FCSTD DOCUMENT  (FreeCAD 0.18R4 (GitTag))
Label: lib_obras_civiles_aeth
License: All rights reserved
LicenseURL: http://en.wikipedia.org/wiki/All_rights_reserved
objects: Part::Part2DObjectPython×84, App::Part×42, App::FeaturePython×21, App::DocumentObjectGroup×11, Spreadsheet::Sheet×4, Part::FeaturePython×4
note: 88 computed .brp shape members not serialized (recipe doc carries the construction recipe); baked Part::Feature solids carry a one-line shape summary decoded from their .brp

FEATURE [Part::Part2DObjectPython] Line001  # Draft 2D object (typed FeaturePython)
  ChamferSize = 0
  Closed = false
  End = (-48.8237,-10,0)
  FilletRadius = 0
  Length = 128.824
  MakeFace = false
  Placement = pos=(80,-10,0) rot=(0,0,1;0rad)
  Points = (2) [(0,-5.32907e-15,0),(-128.824,-3.55271e-15,0)]
  Start = (80,-10,0)
  Subdivisions = 0
FEATURE [Part::Part2DObjectPython] Line  # Draft 2D object (typed FeaturePython)
  ChamferSize = 0
  Closed = false
  End = (-48.9007,10,0)
  FilletRadius = 0
  Length = 128.901
  MakeFace = false
  Placement = pos=(80,10,0) rot=(0,0,1;0rad)
  Points = (2) [(0,0,0),(-128.901,-3.55271e-15,0)]
  Start = (80,10,0)
  Subdivisions = 0
FEATURE [Part::Part2DObjectPython] Circle  # Draft 2D object (typed FeaturePython)
  FirstAngle = 0
  LastAngle = 0
  MakeFace = false
  Radius = 50
FEATURE [Part::Part2DObjectPython] Line003  # Draft 2D object (typed FeaturePython)
  ChamferSize = 0
  Closed = false
  End = (100,100,0)
  FilletRadius = 0
  Length = 91.7357
  MakeFace = false
  Placement = pos=(35.1355,35.1306,0) rot=(0,0,1;0rad)
  Points = (2) [(0,0,0),(64.8645,64.8694,0)]
  Start = (35.1355,35.1306,0)
  Subdivisions = 0
FEATURE [Part::Part2DObjectPython] Rectangle016  label="puerta"  # Draft 2D object (typed FeaturePython)
  ChamferSize = 0
  Columns = 1
  FilletRadius = 0
  Height = 50
  Length = 900
  MakeFace = true
  Rows = 1
FEATURE [Part::Part2DObjectPython] Line004  label="limite_apertura_puerta"  # Draft 2D object (typed FeaturePython)
  ChamferSize = 0
  Closed = false
  End = (0,900,0)
  FilletRadius = 0
  Length = 900
  MakeFace = true
  Points = (2) [(0,0,0),(2.75546e-14,900,0)]
  Start = (0,0,0)
  Subdivisions = 0
FEATURE [Part::Part2DObjectPython] Arc  label="apertura_puerta"  # Draft 2D object (typed FeaturePython)
  FirstAngle = 0
  LastAngle = 90
  MakeFace = true
  Radius = 900
FEATURE [App::DocumentObjectGroup] Group001  label="puerta_generica"
  Group = -> [Rectangle016,Line004,Arc]
FEATURE [App::Part] Part002  label="puerta_90cm__"
  Group = -> [Arc,Rectangle016,Line004,Group001]
  Origin = -> Origin002
FEATURE [Part::Part2DObjectPython] Rectangle017  label="puerta_doble_cuerpo"  # Draft 2D object (typed FeaturePython)
  ChamferSize = 0
  Columns = 1
  FilletRadius = 0
  Height = 50
  Length = 2000
  MakeFace = true
  Rows = 1
FEATURE [Part::Part2DObjectPython] Line005  label="puerta_li"  # Draft 2D object (typed FeaturePython)
  ChamferSize = 0
  Closed = false
  End = (0,1000,0)
  FilletRadius = 0
  Length = 1000
  MakeFace = true
  Points = (2) [(0,0,0),(3.06162e-14,1000,0)]
  Start = (0,0,0)
  Subdivisions = 0
FEATURE [Part::Part2DObjectPython] Line006  label="puerta_ld"  # Draft 2D object (typed FeaturePython)
  ChamferSize = 0
  Closed = false
  End = (2000,1000,0)
  FilletRadius = 0
  Length = 1000
  MakeFace = true
  Placement = pos=(2000,6.12e-14,0) rot=(0,0,1;0rad)
  Points = (2) [(0,0,0),(0,1000,0)]
  Start = (2000,6.12e-14,0)
  Subdivisions = 0
FEATURE [Part::Part2DObjectPython] Arc001  label="arco_ld"  # Draft 2D object (typed FeaturePython)
  FirstAngle = 90
  LastAngle = 180
  MakeFace = true
  Placement = pos=(2000,6.12e-14,0) rot=(0,0,1;0rad)
  Radius = 1000
FEATURE [Part::Part2DObjectPython] Arc002  label="arco_li"  # Draft 2D object (typed FeaturePython)
  FirstAngle = 0
  LastAngle = 90
  MakeFace = true
  Radius = 1000
FEATURE [App::DocumentObjectGroup] Group002  label="puerta_generica_doble"
  Group = -> [Rectangle017,Line005,Line006,Arc001,Arc002]
FEATURE [App::Part] Part003  label="puerta_doble_2m__"
  Group = -> [Rectangle017,Line006,Line005,Arc001,Arc002,Group002]
  Origin = -> Origin003
FEATURE [Part::Part2DObjectPython] Wire001  # Draft 2D object (typed FeaturePython)
  ChamferSize = 0
  Closed = true
  End = (300,100,0)
  FilletRadius = 0
  Length = 716.228
  MakeFace = true
  Points = (3) [(0,0,0),(300,9.18485e-15,0),(300,100,0)]
  Start = (0,0,0)
  Subdivisions = 0
FEATURE [Part::Part2DObjectPython] Wire002  # Draft 2D object (typed FeaturePython)
  ChamferSize = 0
  Closed = true
  End = (300,100,0)
  FilletRadius = 0
  Length = 716.228
  MakeFace = true
  Points = (3) [(0,0,0),(3.06162e-15,100,0),(300,100,0)]
  Start = (0,0,0)
  Subdivisions = 0
FEATURE [Part::Part2DObjectPython] Rectangle039  # Draft 2D object (typed FeaturePython)
  ChamferSize = 0
  Columns = 1
  FilletRadius = 0
  Height = 100
  Length = 100
  MakeFace = true
  Rows = 1
FEATURE [Spreadsheet::Sheet] IfcProperties005  label="caja_2400_df_props"
  cells = A1=parametro; B1=magnitud; C1=unidades; A2=tipo_toma; B2=ciega; C2=n/a; A3=estado; B3=ok; C3=n/a; A4=num_circuito; C4=n/a; A5=num_tablero_distribucion; C5=n/a; A6=altura_desde_piso; C6=m
FEATURE [Part::Part2DObjectPython] Circle007  # Draft 2D object (typed FeaturePython)
  FirstAngle = 0
  LastAngle = 0
  MakeFace = false
  Radius = 50
FEATURE [Part::Part2DObjectPython] Line019  # Draft 2D object (typed FeaturePython)
  ChamferSize = 0
  Closed = false
  End = (-48.9007,10,0)
  FilletRadius = 0
  Length = 128.901
  MakeFace = false
  Placement = pos=(80,10,0) rot=(0,0,1;0rad)
  Points = (2) [(0,0,0),(-128.901,-3.55271e-15,0)]
  Start = (80,10,0)
  Subdivisions = 0
FEATURE [Part::Part2DObjectPython] Line020  # Draft 2D object (typed FeaturePython)
  ChamferSize = 0
  Closed = false
  End = (-48.8237,-10,0)
  FilletRadius = 0
  Length = 128.824
  MakeFace = false
  Placement = pos=(80,-10,0) rot=(0,0,1;0rad)
  Points = (2) [(0,-5.32907e-15,0),(-128.824,-3.55271e-15,0)]
  Start = (80,-10,0)
  Subdivisions = 0
FEATURE [Spreadsheet::Sheet] IfcProperties012  label="tomacorriente_interruptor_props"
  cells = A1=parametro; B1=magnitud; C1=unidades; A2=tipo_toma; C2=n/a; A3=estado; C3=n/a; A4=num_circuito_toma; C4=n/a; A5=num_circuito_interruptor; C5=n/a; A6=num_tablero_distribucion_toma; C6=n/a; A7=num_tablero_distribucion_interruptor; C7=n/a; A8=altura_desde_piso; C8=m
FEATURE [Part::Part2DObjectPython] Line021  # Draft 2D object (typed FeaturePython)
  ChamferSize = 0
  Closed = false
  End = (250,100,0)
  FilletRadius = 0
  Length = 91.7357
  MakeFace = false
  Placement = pos=(185.136,35.1306,0) rot=(0,0,1;0rad)
  Points = (2) [(0,0,0),(64.8645,64.8694,0)]
  Start = (185.136,35.1306,0)
  Subdivisions = 0
FEATURE [Part::Part2DObjectPython] Circle008  # Draft 2D object (typed FeaturePython)
  FirstAngle = 0
  LastAngle = 0
  MakeFace = false
  Placement = pos=(150,0,0) rot=(0,0,1;0rad)
  Radius = 50
FEATURE [Part::Part2DObjectPython] Line025  # Draft 2D object (typed FeaturePython)
  ChamferSize = 0
  Closed = false
  End = (100,100,0)
  FilletRadius = 0
  Length = 91.7357
  MakeFace = false
  Placement = pos=(35.1355,35.1306,0) rot=(0,0,1;0rad)
  Points = (2) [(0,0,0),(64.8645,64.8694,0)]
  Start = (35.1355,35.1306,0)
  Subdivisions = 0
FEATURE [Part::Part2DObjectPython] Circle011  # Draft 2D object (typed FeaturePython)
  FirstAngle = 0
  LastAngle = 0
  MakeFace = false
  Radius = 100
FEATURE [Part::Part2DObjectPython] Line028  # Draft 2D object (typed FeaturePython)
  ChamferSize = 0
  Closed = false
  End = (0,-100,0)
  FilletRadius = 0
  Length = 200
  MakeFace = true
  Placement = pos=(0,100,0) rot=(0,0,1;0rad)
  Points = (2) [(0,0,0),(0,-200,0)]
  Start = (0,100,0)
  Subdivisions = 0
FEATURE [Part::Part2DObjectPython] Line029  # Draft 2D object (typed FeaturePython)
  ChamferSize = 0
  Closed = false
  End = (-100,3.8e-15,0)
  FilletRadius = 0
  Length = 200
  MakeFace = true
  Placement = pos=(100,1.8e-14,0) rot=(0,0,1;0rad)
  Points = (2) [(0,0,0),(-200,-1.42109e-14,0)]
  Start = (100,1.8e-14,0)
  Subdivisions = 0
FEATURE [Part::Part2DObjectPython] Line035  # Draft 2D object (typed FeaturePython)
  ChamferSize = 0
  Closed = false
  End = (0,0,0)
  FilletRadius = 0
  Length = 200
  MakeFace = true
  Placement = pos=(0,200,0) rot=(0,0,1;0rad)
  Points = (2) [(0,0,0),(0,-200,0)]
  Start = (0,200,0)
  Subdivisions = 0
FEATURE [Part::Part2DObjectPython] Arc003  # Draft 2D object (typed FeaturePython)
  FirstAngle = -90
  LastAngle = 90
  MakeFace = true
  Placement = pos=(0,100,0) rot=(0,0,1;0rad)
  Radius = 100
FEATURE [Part::Part2DObjectPython] Line036  # Draft 2D object (typed FeaturePython)
  ChamferSize = 0
  Closed = false
  End = (200,300,0)
  FilletRadius = 0
  Length = 141.421
  MakeFace = true
  Placement = pos=(100,200,0) rot=(0,0,1;0rad)
  Points = (2) [(0,0,0),(100,100,0)]
  Start = (100,200,0)
  Subdivisions = 0
FEATURE [Part::Part2DObjectPython] Line037  # Draft 2D object (typed FeaturePython)
  ChamferSize = 0
  Closed = false
  End = (200,-100,0)
  FilletRadius = 0
  Length = 141.421
  MakeFace = true
  Placement = pos=(100,6.1e-15,0) rot=(0,0,1;0rad)
  Points = (2) [(0,0,0),(100,-100,0)]
  Start = (100,6.1e-15,0)
  Subdivisions = 0
FEATURE [Part::Part2DObjectPython] Line038  # Draft 2D object (typed FeaturePython)
  ChamferSize = 0
  Closed = false
  End = (300,100,0)
  FilletRadius = 0
  Length = 100
  MakeFace = true
  Placement = pos=(200,100,0) rot=(0,0,1;0rad)
  Points = (2) [(0,0,0),(100,-5.68434e-14,0)]
  Start = (200,100,0)
  Subdivisions = 0
FEATURE [App::DocumentObjectGroup] Grupo027  label="caja_2400_df_generica"
  Group = -> [Rectangle039,IfcProperties005]
FEATURE [App::Part] Part009  label="caja_2400_df__"
  Group = -> [Rectangle039,Grupo027,IfcProperties005]
  Origin = -> Origin009
FEATURE [Part::Part2DObjectPython] Rectangle041  # Draft 2D object (typed FeaturePython)
  ChamferSize = 0
  Columns = 1
  FilletRadius = 0
  Height = 60
  Length = 100
  MakeFace = true
  Rows = 1
FEATURE [Spreadsheet::Sheet] IfcProperties037  label="caja_5800_props"
  cells = A1=parametro; B1=magnitud; C1=unidades; A2=tipo_toma; B2=ciega; C2=n/a; A3=estado; B3=n/d; C3=n/a; A4=num_circuito; B4=n/d; C4=n/a; A5=num_tablero_distribucion; B5=n/d; C5=n/a; A6=altura_desde_piso; C6=m
FEATURE [App::DocumentObjectGroup] Grupo056  label="caja_5800_generica"
  Group = -> [Rectangle041,IfcProperties037]
FEATURE [App::Part] Part041  label="caja_5800___"
  Group = -> [Rectangle041,Grupo056,IfcProperties037]
  Origin = -> Origin041
FEATURE [Part::Part2DObjectPython] Rectangle043  # Draft 2D object (typed FeaturePython)
  ChamferSize = 0
  Columns = 1
  FilletRadius = 0
  Height = 100
  Length = 100
  MakeFace = true
  Rows = 1
FEATURE [Spreadsheet::Sheet] IfcProperties039  label="caja_2400_props"
  cells = A1=parametro; B1=magnitud; C1=unidades; A2=tipo_toma; B2=ciega; C2=n/a; A3=estado; B3=ok; C3=n/a; A4=num_circuito; C4=n/a; A5=num_tablero_distribucion; C5=n/a; A6=altura_desde_piso; C6=m
FEATURE [App::DocumentObjectGroup] Grupo058  label="caja_2400_generica"
  Group = -> [Rectangle043,IfcProperties039]
FEATURE [App::Part] Part043  label="caja_2400__"
  Group = -> [Rectangle043,Grupo058,IfcProperties039]
  Origin = -> Origin043
FEATURE [Part::Part2DObjectPython] Rectangle048  label="luz_30x120_cuerpo"  # Draft 2D object (typed FeaturePython)
  ChamferSize = 0
  Columns = 1
  FilletRadius = 0
  Height = 300
  Length = 1200
  MakeFace = true
  Rows = 1
FEATURE [Part::Part2DObjectPython] Circle051  # Draft 2D object (typed FeaturePython)
  FirstAngle = 0
  LastAngle = 0
  MakeFace = true
  Radius = 100
FEATURE [Part::Part2DObjectPython] Line124  # Draft 2D object (typed FeaturePython)
  ChamferSize = 0
  Closed = false
  End = (0,-100,0)
  FilletRadius = 0
  Length = 200
  MakeFace = true
  Placement = pos=(0,100,0) rot=(0,0,1;0rad)
  Points = (2) [(0,0,0),(0,-200,0)]
  Start = (0,100,0)
  Subdivisions = 0
FEATURE [Part::Part2DObjectPython] Line125  # Draft 2D object (typed FeaturePython)
  ChamferSize = 0
  Closed = false
  End = (-100,3.8e-15,0)
  FilletRadius = 0
  Length = 200
  MakeFace = true
  Placement = pos=(100,1.8e-14,0) rot=(0,0,1;0rad)
  Points = (2) [(0,0,0),(-200,-1.42109e-14,0)]
  Start = (100,1.8e-14,0)
  Subdivisions = 0
FEATURE [Part::Part2DObjectPython] Circle052  label="datos_techo_base"  # Draft 2D object (typed FeaturePython)
  FirstAngle = 0
  LastAngle = 0
  MakeFace = false
  Radius = 50
FEATURE [Part::Part2DObjectPython] Polygon  label="datos_base"  # Draft 2D object (typed FeaturePython)
  ChamferSize = 0
  DrawMode = 0
  FacesNumber = 3
  FilletRadius = 0
  MakeFace = true
  Placement = pos=(0,0,0) rot=(0,0,1;1.5708rad)
  Radius = 50.47
FEATURE [Part::Part2DObjectPython] Polygon001  label="datos_base001"  # Draft 2D object (typed FeaturePython)
  ChamferSize = 0
  DrawMode = 0
  FacesNumber = 3
  FilletRadius = 0
  MakeFace = true
  Placement = pos=(0,0,0) rot=(0,0,1;1.5708rad)
  Radius = 50.47
FEATURE [Part::Part2DObjectPython] Polygon002  label="datos_base002"  # Draft 2D object (typed FeaturePython)
  ChamferSize = 0
  DrawMode = 0
  FacesNumber = 3
  FilletRadius = 0
  MakeFace = true
  Placement = pos=(0,0,0) rot=(0,0,1;1.5708rad)
  Radius = 50.47
FEATURE [Part::Part2DObjectPython] Circle053  label="datos_techo_base001"  # Draft 2D object (typed FeaturePython)
  FirstAngle = 0
  LastAngle = 0
  MakeFace = false
  Radius = 50
FEATURE [App::Part] Part085  label="datos_techo__"
  Group = -> [Polygon002,Circle053]
  Origin = -> Origin085
FEATURE [Part::Part2DObjectPython] Rectangle  label="datos_piso_base"  # Draft 2D object (typed FeaturePython)
  ChamferSize = 0
  Columns = 1
  FilletRadius = 0
  Height = 100
  Length = 100
  MakeFace = false
  Placement = pos=(-50,-40,0) rot=(0,0,1;0rad)
  Rows = 1
FEATURE [App::DocumentObjectGroup] Group013  label="piezas_red_datos_base__"
  Group = -> [Polygon,Circle052,Rectangle]
FEATURE [Part::Part2DObjectPython] Rectangle049  label="datos_piso_base001"  # Draft 2D object (typed FeaturePython)
  ChamferSize = 0
  Columns = 1
  FilletRadius = 0
  Height = 100
  Length = 100
  MakeFace = false
  Placement = pos=(-50,-40,0) rot=(0,0,1;0rad)
  Rows = 1
FEATURE [Part::Part2DObjectPython] Polygon003  label="datos_base003"  # Draft 2D object (typed FeaturePython)
  ChamferSize = 0
  DrawMode = 0
  FacesNumber = 3
  FilletRadius = 0
  MakeFace = true
  Placement = pos=(0,0,0) rot=(0,0,1;1.5708rad)
  Radius = 50.47
FEATURE [App::Part] Part086  label="datos_piso__"
  Group = -> [Rectangle049,Polygon003]
  Origin = -> Origin086
FEATURE [App::FeaturePython] InternalObjectName  label="tc_props"  # WARN: FeaturePython — macro-defined, semantics opaque (R4)
  altura_desde_piso = 0
  cantidad_puertos = 2
  corriente_max_a = 15
  nombre_propiedad_exportable = tomacorriente_propiedades
  tipo = NEMA 5-15R
  voltaje_max_v = 250
FEATURE [Part::Part2DObjectPython] Rectangle047  label="canaleta_base_001"  # Draft 2D object (typed FeaturePython)
  ChamferSize = 0
  Columns = 1
  FilletRadius = 0
  Height = 2400
  Length = 50
  MakeFace = true
  Rows = 1
FEATURE [App::FeaturePython] InternalObjectName001  label="canaleta_120x50_propiedades_001"  # WARN: FeaturePython — macro-defined, semantics opaque (R4)
  nombre_propiedad_exportable = canaleta_electrica_propiedades
  tipo = Canaleta metálica 120 mm x 50 mm
FEATURE [App::Part] Part087  label="canaleta_120x50__"
  Group = -> [Rectangle047,InternalObjectName001]
  Origin = -> Origin087
FEATURE [App::FeaturePython] InternalObjectName002  label="td_props"  # WARN: FeaturePython — macro-defined, semantics opaque (R4)
  altura_desde_piso = 0
  corriente_max_fase_a = 0
  nombre_propiedad_exportable = tablero_distribucion_propiedades
  num_circuitos = 9
  num_fases = 3
  voltaje_max_fase_v = 0
FEATURE [App::DocumentObjectGroup] Group015  label="piezas_canalizacion_cableado"
  Group = -> [Part087,Part009,Part041,Part043]
FEATURE [Part::Part2DObjectPython] Rectangle003  # Draft 2D object (typed FeaturePython)
  ChamferSize = 0
  Columns = 1
  FilletRadius = 0
  Height = 250
  Length = 900
  MakeFace = true
  Placement = pos=(-8e-15,250,0) rot=(0,0,1;0rad)
  Rows = 1
FEATURE [Part::Part2DObjectPython] Rectangle002  # Draft 2D object (typed FeaturePython)
  ChamferSize = 0
  Columns = 1
  FilletRadius = 0
  Height = 250
  Length = 900
  MakeFace = true
  Rows = 1
FEATURE [Part::Part2DObjectPython] Rectangle008  # Draft 2D object (typed FeaturePython)
  ChamferSize = 0
  Columns = 1
  FilletRadius = 0
  Height = 2200
  Length = 900
  MakeFace = true
  Rows = 1
FEATURE [Part::Part2DObjectPython] Rectangle004  # Draft 2D object (typed FeaturePython)
  ChamferSize = 0
  Columns = 1
  FilletRadius = 0
  Height = 250
  Length = 900
  MakeFace = true
  Placement = pos=(-8e-15,500,0) rot=(0,0,1;0rad)
  Rows = 1
FEATURE [Part::Part2DObjectPython] Rectangle005  # Draft 2D object (typed FeaturePython)
  ChamferSize = 0
  Columns = 1
  FilletRadius = 0
  Height = 250
  Length = 900
  MakeFace = true
  Placement = pos=(-8e-15,750,0) rot=(0,0,1;0rad)
  Rows = 1
FEATURE [Part::Part2DObjectPython] Rectangle006  # Draft 2D object (typed FeaturePython)
  ChamferSize = 0
  Columns = 1
  FilletRadius = 0
  Height = 250
  Length = 900
  MakeFace = true
  Placement = pos=(-8e-15,1000,0) rot=(0,0,1;0rad)
  Rows = 1
FEATURE [Part::Part2DObjectPython] Line129  # Draft 2D object (typed FeaturePython)
  ChamferSize = 0
  Closed = false
  End = (2.274e-13,2200,0)
  FilletRadius = 0
  Length = 1140.18
  MakeFace = true
  Placement = pos=(900,1500,0) rot=(0,0,1;0rad)
  Points = (2) [(0,0,0),(-900,700,0)]
  Start = (900,1500,0)
  Subdivisions = 0
FEATURE [Part::Part2DObjectPython] Rectangle007  # Draft 2D object (typed FeaturePython)
  ChamferSize = 0
  Columns = 1
  FilletRadius = 0
  Height = 250
  Length = 900
  MakeFace = true
  Placement = pos=(-8e-15,1250,0) rot=(0,0,1;0rad)
  Rows = 1
FEATURE [App::Part] Part088  label="escaleras_90cm__"
  Group = -> [Rectangle002,Rectangle003,Rectangle004,Rectangle005,Rectangle006,Rectangle007,Rectangle008,Line129]
  Origin = -> Origin088
FEATURE [App::DocumentObjectGroup] Grupo011  label="piezas_civil"
  Group = -> [Part002,Part003,Part088]
FEATURE [Part::Part2DObjectPython] Rectangle050  label="luz_60x60_cuerpo001"  # Draft 2D object (typed FeaturePython)
  ChamferSize = 0
  Columns = 1
  FilletRadius = 0
  Height = 600
  Length = 600
  MakeFace = true
  Rows = 1
FEATURE [App::FeaturePython] InternalObjectName003  label="luz_60x60_props"  # WARN: FeaturePython — macro-defined, semantics opaque (R4)
  altura_desde_piso = 0
  nombre_propiedad_exportable = luz_propiedades
  potencia_w = 0
  voltaje_max_v = 130
  voltaje_min_v = 95
  voltaje_nominal_v = 110
FEATURE [App::FeaturePython] InternalObjectName004  label="i1_propiedades"  # WARN: FeaturePython — macro-defined, semantics opaque (R4)
  altura_desde_piso = 0
  corriente_max_a = 10
  nombre_propiedad_exportable = interruptor_propiedades
  tipo_interruptor = Ordinario sencillo
  voltaje_max_v = 250
FEATURE [App::FeaturePython] InternalObjectName005  label="i2_props"  # WARN: FeaturePython — macro-defined, semantics opaque (R4)
  altura_desde_piso = 0
  corriente_max_int1_a = 0
  corriente_max_int2_a = 0
  nombre_propiedad_exportable = interruptor2_propiedades
  voltaje_max_int1_v = 0
  voltaje_max_int2_v = 0
FEATURE [Part::Part2DObjectPython] Circle054  # Draft 2D object (typed FeaturePython)
  FirstAngle = 0
  LastAngle = 0
  MakeFace = false
  Radius = 50
FEATURE [Part::Part2DObjectPython] Circle055  # Draft 2D object (typed FeaturePython)
  FirstAngle = 0
  LastAngle = 0
  MakeFace = false
  Radius = 50
FEATURE [Part::Part2DObjectPython] Line130  # Draft 2D object (typed FeaturePython)
  ChamferSize = 0
  Closed = false
  End = (100,100,0)
  FilletRadius = 0
  Length = 91.7357
  MakeFace = false
  Placement = pos=(35.1355,35.1306,0) rot=(0,0,1;0rad)
  Points = (2) [(0,0,0),(64.8645,64.8694,0)]
  Start = (35.1355,35.1306,0)
  Subdivisions = 0
FEATURE [App::FeaturePython] InternalObjectName006  label="i3_props"  # WARN: FeaturePython — macro-defined, semantics opaque (R4)
  altura_desde_piso = 0
  corriente_max_int1_a = 0
  corriente_max_int2_a = 0
  corriente_max_int3_a = 0
  nombre_propiedad_exportable = interruptor3_propiedades
  voltaje_max_int1_v = 0
  voltaje_max_int2_v = 0
  voltaje_max_int3_v = 0
FEATURE [Part::Part2DObjectPython] Circle056  # Draft 2D object (typed FeaturePython)
  FirstAngle = 0
  LastAngle = 0
  MakeFace = false
  Radius = 50
FEATURE [App::FeaturePython] InternalObjectName007  label="td_propiedades"  # WARN: FeaturePython — macro-defined, semantics opaque (R4)
  altura_desde_piso = 0
  nombre_propiedad_exportable = toma_datos_propiedades
FEATURE [Part::Part2DObjectPython] Polygon004  label="datos_base004"  # Draft 2D object (typed FeaturePython)
  ChamferSize = 0
  DrawMode = 0
  FacesNumber = 3
  FilletRadius = 0
  MakeFace = true
  Placement = pos=(0,0,0) rot=(0,0,1;1.5708rad)
  Radius = 50.47
FEATURE [App::FeaturePython] InternalObjectName008  label="td2_propiedades"  # WARN: FeaturePython — macro-defined, semantics opaque (R4)
  altura_desde_piso = 0
  nombre_propiedad_exportable = toma_datos_doble_propiedades
FEATURE [App::Part] Part091  label="datos_pared_doble__"
  Group = -> [Polygon004,InternalObjectName008]
  Origin = -> Origin091
FEATURE [App::FeaturePython] Text  label="puerto"  # WARN: FeaturePython — macro-defined, semantics opaque (R4)
  Placement = pos=(-147.699,121.529,0) rot=(0,0,1;0rad)
  Text = 5
  id_pieza_electronica_asociada = 0x423dc7d37fb7f75e6ff6c4be87a5650f41ce93914b7fe7c281abe934e83abca7564aa2305079aadd4d82ee029343f79464a1570b213fab293269607f9b94dc1b
  propiedad_pieza_electronica = puerto_dispositivo_fuente_datos
FEATURE [App::Part] Part084  label="datos_pared_sencilla__"
  Group = -> [Polygon001,InternalObjectName007,Text]
  Origin = -> Origin084
FEATURE [App::DocumentObjectGroup] Group012  label="piezas_red_datos"
  Group = -> [Part084,Group013,Part085,Part086,Part091]
FEATURE [App::FeaturePython] InternalObjectName009  label="ti_props"  # WARN: FeaturePython — macro-defined, semantics opaque (R4)
  altura_desde_piso = 0
  corriente_max_int_a = 0
  corriente_max_tc_a = 0
  nombre_propiedad_exportable = interruptor_tomacorriente_propiedades
  tipo_interruptor = Sencillo
  tipo_tomacorriente = NEMA 5-15R
  voltaje_max_int_v = 0
  voltaje_max_tc_v = 0
FEATURE [App::Part] Part092  label="contenido001"
  Group = -> [Line003,Circle054]
  Origin = -> Origin092
FEATURE [App::Part] Part093  label="contenido002"
  Group = -> [Circle007,Line019,Line020,IfcProperties012,Line021,Circle008]
  Origin = -> Origin093
FEATURE [App::FeaturePython] InternalObjectName010  label="luz_8in_props"  # WARN: FeaturePython — macro-defined, semantics opaque (R4)
  altura_desde_piso = 0
  nombre_propiedad_exportable = luz_propiedades
  potencia_w = 18
  tipo_luz = Led
  voltaje_max_v = 130
  voltaje_min_v = 95
  voltaje_nominal_v = 110
FEATURE [App::Part] Part095  label="contenido004"
  Group = -> [Circle011,Line028,Line029]
  Origin = -> Origin095
  Placement = pos=(0,0,0) rot=(0,0,1;0.785398rad)
FEATURE [App::Part] Part096  label="contenido005"
  Group = -> [Line035,Arc003,Line036,Line037,Line038]
  Origin = -> Origin096
FEATURE [App::Part] Part097  label="contenido006"
  Group = -> [Rectangle048]
  Origin = -> Origin097
FEATURE [App::Part] Part098  label="contenido007"
  Group = -> [Circle051,Line124,Line125]
  Origin = -> Origin098
FEATURE [App::Part] Part099  label="contenido008"
  Group = -> [Circle,Line,Line001]
  Origin = -> Origin099
FEATURE [App::Part] Part100  label="contenido009"
  Group = -> [Wire002,Wire001]
  Origin = -> Origin100
FEATURE [App::Part] Part101  label="contenido"
  Group = -> [Rectangle050]
  Origin = -> Origin101
FEATURE [App::FeaturePython] InternalObjectName014  label="luz_tortuga_props"  # WARN: FeaturePython — macro-defined, semantics opaque (R4)
  altura_desde_piso = 0
  nombre_propiedad_exportable = luz_propiedades
  potencia_w = 25
  tipo_luz = Plasma
  voltaje_max_v = 130
  voltaje_min_v = 95
  voltaje_nominal_v = 110
FEATURE [App::FeaturePython] InternalObjectName015  label="luz_30x120_props"  # WARN: FeaturePython — macro-defined, semantics opaque (R4)
  altura_desde_piso = 0
  nombre_propiedad_exportable = luz_propiedades
  potencia_w = 48
  tipo_luz = Led
  voltaje_max_v = 130
  voltaje_min_v = 95
  voltaje_nominal_v = 110
FEATURE [App::FeaturePython] InternalObjectName016  label="luz_roseta_props"  # WARN: FeaturePython — macro-defined, semantics opaque (R4)
  altura_desde_piso = 0
  nombre_propiedad_exportable = luz_propiedades
  potencia_w = 25
  tipo_luz = Plasma
  voltaje_max_v = 130
  voltaje_min_v = 95
  voltaje_nominal_v = 110
FEATURE [App::Part] Part081  label="luz_roseta__"
  Group = -> [Part098,InternalObjectName016]
  Origin = -> Origin081
  Placement = pos=(0,0,0) rot=(0,0,1;0.785398rad)
FEATURE [App::FeaturePython] InternalObjectName017  label="luz_6.5in_props"  # WARN: FeaturePython — macro-defined, semantics opaque (R4)
  altura_desde_piso = 0
  nombre_propiedad_exportable = luz_propiedades
  potencia_w = 18
  tipo_luz = Led
  voltaje_max_v = 130
  voltaje_min_v = 95
  voltaje_nominal_v = 110
FEATURE [Part::Part2DObjectPython] Circle057  # Draft 2D object (typed FeaturePython)
  FirstAngle = 0
  LastAngle = 0
  MakeFace = false
  Radius = 82.5
FEATURE [Part::Part2DObjectPython] Line131  # Draft 2D object (typed FeaturePython)
  ChamferSize = 0
  Closed = false
  End = (0,-82.5,0)
  FilletRadius = 0
  Length = 165
  MakeFace = true
  Placement = pos=(0,82.5,0) rot=(0,0,1;0rad)
  Points = (2) [(0,0,0),(0,-165,0)]
  Start = (0,82.5,0)
  Subdivisions = 0
FEATURE [Part::Part2DObjectPython] Line132  # Draft 2D object (typed FeaturePython)
  ChamferSize = 0
  Closed = false
  End = (82.5,-6.51e-14,0)
  FilletRadius = 0
  Length = 165
  MakeFace = true
  Placement = pos=(-82.5,0,0) rot=(0,0,1;1.5708rad)
  Points = (2) [(0,0,0),(-2.84217e-14,-165,0)]
  Start = (-82.5,0,0)
  Subdivisions = 0
FEATURE [App::Part] Part102  label="contenido010"
  Group = -> [Circle057,Line131,Line132]
  Origin = -> Origin103
  Placement = pos=(0,0,0) rot=(0,0,1;0.785398rad)
FEATURE [App::FeaturePython] InternalObjectName018  label="cbk_propiedades"  # WARN: FeaturePython — macro-defined, semantics opaque (R4)
  corriente_max_a = 10
  nombre_propiedad_exportable = disyuntor_propiedades
  voltaje_max_v = 600
FEATURE [App::Part] Part104  label="cbk__"
  Group = -> [InternalObjectName018]
  Origin = -> Origin104
FEATURE [App::FeaturePython] InternalObjectName019  label="cbk2_propiedades"  # WARN: FeaturePython — macro-defined, semantics opaque (R4)
  corriente_max_a = 10
  nombre_propiedad_exportable = disyuntor2_propiedades
  voltaje_max_v = 240
FEATURE [App::Part] Part105  label="cbk2__"
  Group = -> [InternalObjectName019]
  Origin = -> Origin105
FEATURE [App::FeaturePython] InternalObjectName020  label="cbk3_propiedades"  # WARN: FeaturePython — macro-defined, semantics opaque (R4)
  corriente_max_a = 10
  nombre_propiedad_exportable = disyuntor3_propiedades
  voltaje_max_v = 240
FEATURE [App::Part] Part106  label="cbk3__"
  Group = -> [InternalObjectName020]
  Origin = -> Origin106
FEATURE [Part::Part2DObjectPython] Circle058  # Draft 2D object (typed FeaturePython)
  FirstAngle = 0
  LastAngle = 0
  MakeFace = false
  Radius = 50
FEATURE [Part::Part2DObjectPython] Arc004  # Draft 2D object (typed FeaturePython)
  FirstAngle = -90
  LastAngle = 90
  MakeFace = true
  Placement = pos=(20,0,0) rot=(0,0,1;0rad)
  Radius = 10
FEATURE [Part::Part2DObjectPython] Arc005  # Draft 2D object (typed FeaturePython)
  FirstAngle = -90
  LastAngle = 90
  MakeFace = true
  Placement = pos=(10,0,0) rot=(0,0,1;0rad)
  Radius = 10
FEATURE [Part::Part2DObjectPython] Line133  # Draft 2D object (typed FeaturePython)
  ChamferSize = 0
  Closed = false
  End = (-20,10,0)
  FilletRadius = 0
  Length = 14.1421
  MakeFace = true
  Placement = pos=(-30,0,0) rot=(0,0,1;0rad)
  Points = (2) [(0,0,0),(10,10,0)]
  Start = (-30,0,0)
  Subdivisions = 0
FEATURE [Part::Part2DObjectPython] Line134  # Draft 2D object (typed FeaturePython)
  ChamferSize = 0
  Closed = false
  End = (-40,0,0)
  FilletRadius = 0
  Length = 10
  MakeFace = true
  Placement = pos=(-30,0,0) rot=(0,0,1;0rad)
  Points = (2) [(0,0,0),(-10,0,0)]
  Start = (-30,0,0)
  Subdivisions = 0
FEATURE [Part::Part2DObjectPython] Line135  # Draft 2D object (typed FeaturePython)
  ChamferSize = 0
  Closed = false
  End = (-10,0,0)
  FilletRadius = 0
  Length = 10
  MakeFace = true
  Placement = pos=(-20,0,0) rot=(0,0,1;0rad)
  Points = (2) [(0,0,0),(10,0,0)]
  Start = (-20,0,0)
  Subdivisions = 0
FEATURE [Part::FeaturePython] Point  # WARN: FeaturePython — macro-defined, semantics opaque (R4)
  X = -20
  Y = 10
  Z = 0
FEATURE [Part::FeaturePython] Point001  # WARN: FeaturePython — macro-defined, semantics opaque (R4)
  X = -20
  Y = 0
  Z = 0
FEATURE [Part::FeaturePython] Point002  # WARN: FeaturePython — macro-defined, semantics opaque (R4)
  X = -10
  Y = 0
  Z = 0
FEATURE [Part::FeaturePython] Point003  # WARN: FeaturePython — macro-defined, semantics opaque (R4)
  X = -40
  Y = 0
  Z = 0
FEATURE [App::Part] Part108  label="contenido011"
  Group = -> [Circle058,Arc004,Arc005,Line133,Line134,Line135,Point,Point001,Point002,Point003]
  Origin = -> Origin108
FEATURE [App::FeaturePython] InternalObjectName021  label="smi_propiedades"  # WARN: FeaturePython — macro-defined, semantics opaque (R4)
  altura_desde_piso = 0
  corriente_max_int_a = 0
  nombre_propiedad_exportable = sensor_movimiento_interruptor_propiedades
  tipo_interruptor = Ordinario sencillo
  voltaje_max_ctrl_v = 0
  voltaje_max_int_v = 0
  voltaje_min_ctrl_v = 0
  voltaje_nominal_ctrl_v = 0
FEATURE [Part::Part2DObjectPython] Circle059  # Draft 2D object (typed FeaturePython)
  FirstAngle = 0
  LastAngle = 0
  MakeFace = false
  Radius = 50
FEATURE [App::FeaturePython] InternalObjectName022  label="extractor_aire_props"  # WARN: FeaturePython — macro-defined, semantics opaque (R4)
  altura_desde_piso = 0
  nombre_propiedad_exportable = extractor_aire_propiedades
  potencia_w = 60
  tipo = Extractor de aire
  voltaje_max_v = 130
  voltaje_min_v = 95
  voltaje_nominal_v = 110
FEATURE [Part::Part2DObjectPython] ShapeString  label="rotulo_dibujo_tecnico__"  # Draft 2D object (typed FeaturePython)
  FontFile = <path>
  Placement = pos=(0,100,0) rot=(0,0,1;0rad)
  Size = 50
  String = -
  Tracking = 0
FEATURE [App::Part] Part  label="tomacorriente__"
  Group = -> [InternalObjectName,Part099,ShapeString]
  Origin = -> Origin
FEATURE [Part::Part2DObjectPython] ShapeString001  label="rotulo_dibujo_tecnico__001"  # Draft 2D object (typed FeaturePython)
  FontFile = <path>
  Placement = pos=(0,100,0) rot=(0,0,1;0rad)
  Size = 50
  String = -
  Tracking = 0
FEATURE [App::Part] Part001  label="interruptor_sencillo__"
  Group = -> [InternalObjectName004,Part092,ShapeString001]
  Origin = -> Origin001
FEATURE [Part::Part2DObjectPython] ShapeString002  label="rotulo_dibujo_tecnico__002"  # Draft 2D object (typed FeaturePython)
  FontFile = <path>
  Placement = pos=(0,100,0) rot=(0,0,1;0rad)
  Size = 50
  String = -
  Tracking = 0
FEATURE [App::Part] Part016  label="tomacorriente_interruptor__"
  Group = -> [InternalObjectName009,Part093,ShapeString002]
  Origin = -> Origin016
FEATURE [Part::Part2DObjectPython] ShapeString003  label="rotulo_dibujo_tecnico__003"  # Draft 2D object (typed FeaturePython)
  FontFile = <path>
  Placement = pos=(0,100,0) rot=(0,0,1;0rad)
  Size = 50
  String = -
  Tracking = 0
FEATURE [Part::Part2DObjectPython] ShapeString004  label="texto"  # Draft 2D object (typed FeaturePython)
  FontFile = <path>
  Placement = pos=(120.626,2.18695,0) rot=(0,0,1;0rad)
  Size = 40
  String = x2
  Tracking = 0
FEATURE [App::Part] Part094  label="contenido003"
  Group = -> [Line025,Circle055,ShapeString004]
  Origin = -> Origin094
FEATURE [App::Part] Part018  label="interruptor_doble__"
  Group = -> [InternalObjectName005,Part094,ShapeString003]
  Origin = -> Origin018
FEATURE [Part::Part2DObjectPython] ShapeString005  label="rotulo_dibujo_tecnico__004"  # Draft 2D object (typed FeaturePython)
  FontFile = <path>
  Placement = pos=(76.2977,137.666,0) rot=(0,0,1;0rad)
  Size = 50
  String = -
  Tracking = 0
FEATURE [App::Part] Part021  label="luz_8in__"
  Group = -> [InternalObjectName010,Part095,ShapeString005]
  Origin = -> Origin021
FEATURE [Part::Part2DObjectPython] ShapeString006  label="rotulo_dibujo_tecnico__005"  # Draft 2D object (typed FeaturePython)
  FontFile = <path>
  Placement = pos=(320.377,295.833,0) rot=(0,0,1;0rad)
  Size = 50
  String = -
  Tracking = 0
FEATURE [App::Part] Part025  label="luz_tortuga__"
  Group = -> [Part096,InternalObjectName014,ShapeString006]
  Origin = -> Origin025
FEATURE [Part::Part2DObjectPython] ShapeString007  label="rotulo_dibujo_tecnico__006"  # Draft 2D object (typed FeaturePython)
  FontFile = <path>
  Placement = pos=(516.126,424.66,0) rot=(0,0,1;0rad)
  Size = 50
  String = -
  Tracking = 0
FEATURE [App::Part] Part066  label="luz_30x120__"
  Group = -> [Part097,InternalObjectName015,ShapeString007]
  Origin = -> Origin066
FEATURE [Part::Part2DObjectPython] ShapeString008  label="rotulo_dibujo_tecnico__007"  # Draft 2D object (typed FeaturePython)
  FontFile = <path>
  Placement = pos=(128.327,160.558,0) rot=(0,0,1;0rad)
  Size = 50
  String = -
  Tracking = 0
FEATURE [App::Part] Part004  label="tablero_distribucion__"
  Group = -> [Part100,InternalObjectName002,ShapeString008]
  Origin = -> Origin004
FEATURE [Part::Part2DObjectPython] ShapeString009  label="rotulo_dibujo_tecnico__008"  # Draft 2D object (typed FeaturePython)
  FontFile = <path>
  Placement = pos=(253.9,699.372,0) rot=(0,0,1;0rad)
  Size = 50
  String = -
  Tracking = 0
FEATURE [App::Part] Part089  label="luz_60x60__"
  Group = -> [InternalObjectName003,Part101,ShapeString009]
  Origin = -> Origin089
FEATURE [Part::Part2DObjectPython] ShapeString010  label="rotulo_dibujo_tecnico__009"  # Draft 2D object (typed FeaturePython)
  FontFile = <path>
  Placement = pos=(0,100,0) rot=(0,0,1;0rad)
  Size = 50
  String = -
  Tracking = 0
FEATURE [Part::Part2DObjectPython] ShapeString011  label="texto001"  # Draft 2D object (typed FeaturePython)
  FontFile = <path>
  Placement = pos=(141.437,8.43031,0) rot=(0,0,1;0rad)
  Size = 40
  String = x3
  Tracking = 0
FEATURE [App::Part] Part111  label="contenido013"
  Group = -> [Line130,Circle056,ShapeString011]
  Origin = -> Origin111
FEATURE [App::Part] Part090  label="interruptor_triple__"
  Group = -> [InternalObjectName006,ShapeString010,Part111]
  Origin = -> Origin090
FEATURE [Part::Part2DObjectPython] ShapeString012  label="rotulo_dibujo_tecnico__010"  # Draft 2D object (typed FeaturePython)
  FontFile = <path>
  Placement = pos=(103.353,118.935,0) rot=(0,0,1;0rad)
  Size = 50
  String = -
  Tracking = 0
FEATURE [App::Part] Part103  label="luz_6.5in__"
  Group = -> [InternalObjectName017,Part102,ShapeString012]
  Origin = -> Origin102
FEATURE [Part::Part2DObjectPython] ShapeString013  label="rotulo_dibujo_tecnico__011"  # Draft 2D object (typed FeaturePython)
  FontFile = <path>
  Placement = pos=(0,100,0) rot=(0,0,1;0rad)
  Size = 50
  String = -
  Tracking = 0
FEATURE [App::Part] Part107  label="sensor_movimiento_interruptor__"
  Group = -> [Part108,InternalObjectName021,ShapeString013]
  Origin = -> Origin107
FEATURE [Part::Part2DObjectPython] ShapeString014  label="rotulo_dibujo_tecnico__012"  # Draft 2D object (typed FeaturePython)
  FontFile = <path>
  Placement = pos=(0,100,0) rot=(0,0,1;0rad)
  Size = 50
  String = -
  Tracking = 0
FEATURE [Part::Part2DObjectPython] ShapeString015  label="texto002"  # Draft 2D object (typed FeaturePython)
  FontFile = <path>
  Placement = pos=(-17.6556,-26.508,0) rot=(0,0,1;0rad)
  Size = 30
  String = F
  Tracking = 0
FEATURE [App::Part] Part110  label="contenido012"
  Group = -> [Circle059,ShapeString015]
  Origin = -> Origin110
FEATURE [App::Part] Part109  label="extractor_aire__"
  Group = -> [Part110,InternalObjectName022,ShapeString014]
  Origin = -> Origin109
FEATURE [App::DocumentObjectGroup] Grupo002  label="piezas_electricas"
  Group = -> [Part001,Part016,Part018,Part021,Part025,Part066,Part081,Part,Part004,Part089,Part090,Part103,Part104,Part105,Part106,Part107,Part109]
FEATURE [App::DocumentObjectGroup] Group014  label="piezas_electronica"
  Group = -> [Group012,Grupo002,Group015]
note: 16 file-system paths scrubbed to <path> (originals preserved in the JSON sidecar)
